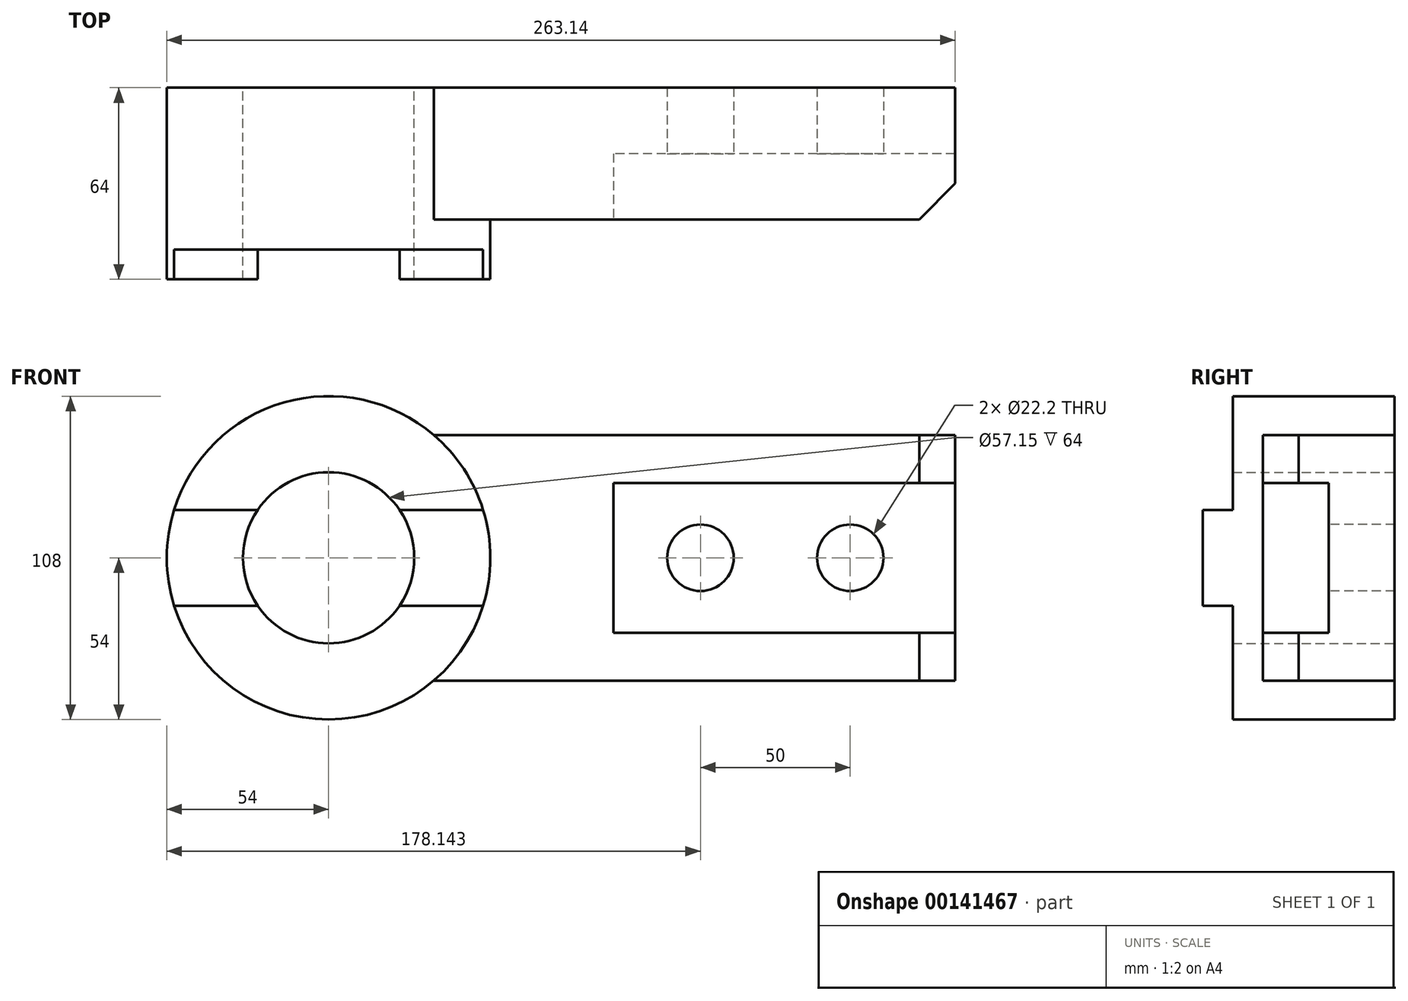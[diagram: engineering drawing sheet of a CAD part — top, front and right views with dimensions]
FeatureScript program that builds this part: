
annotation { "Feature Type Name" : "Feature", "Feature Type Description" : "" }
export const myFeature = defineFeature(function(context is Context, id is Id, definition is map)
    precondition{}
    {
        {
            var Q0;
            Q0=qCreatedBy(makeId("Front.planeOp"),FACE);
            var sketch = newSketch(context, id + "F0", { "sketchPlane" : qUnion([Q0])});
            skCircle(sketch, "E0", {"center": v(0, 0) * mm, "radius": 28.57 * mm});
            skCircle(sketch, "E1", {"center": v(0, 0) * mm, "radius": 54 * mm});
            skLineSegment(sketch, "E2", {"start": v(35.14, 41) * mm, "end": v(209.14, 41) * mm});
            skLineSegment(sketch, "E3", {"start": v(209.14, 41) * mm, "end": v(209.14, -41) * mm});
            skLineSegment(sketch, "E4", {"start": v(209.14, -41) * mm, "end": v(35.14, -41) * mm});
            skSolve(sketch);
        }
        {
            var Q0;
            Q0=makeQuery(id+"F0.imprint","IMPRINT",FACE,{"disambiguationData":[TD([[makeQuery(id+"F0.imprint","IMPRINT",EDGE,{"derivedFrom":sQuery(id+"F0.wireOp",EDGE,"E0")}),-1.0]])]});
            extrude(context, id + "F1", {"entities" : qUnion([Q0]), "depth" : 64 * mm});
        }
        {
            var Q0;
            {var subQ0=sQuery(id+"F0.wireOp",EDGE,"E2");Q0=makeQuery(id+"F0.imprint","IMPRINT",FACE,{"disambiguationData":[TD([[makeQuery(id+"F0.imprint","IMPRINT",EDGE,{"derivedFrom":subQ0}),-1.0]])]});}
            extrude(context, id + "F2", {"entities" : qUnion([Q0]), "operationType" : NewBodyOperationType.ADD, "depth" : 44 * mm});
        }
        {
            var Q0;
            Q0=makeQuery(id+"F2.opExtrude","CAP_FACE",FACE,{"disambiguationData":[OSD([sQuery(id+"F0.wireOp",EDGE,"E1"),sQuery(id+"F0.wireOp",EDGE,"E2"),sQuery(id+"F0.wireOp",EDGE,"E3"),sQuery(id+"F0.wireOp",EDGE,"E4")])],"isStart":false});
            var sketch = newSketch(context, id + "F3", { "sketchPlane" : qUnion([Q0])});
            skLineSegment(sketch, "E5", {"start": v(209.14, -41) * mm, "end": v(209.14, -25) * mm});
            skLineSegment(sketch, "E6", {"start": v(209.14, -25) * mm, "end": v(95.14, -25) * mm});
            skLineSegment(sketch, "E7", {"start": v(95.14, -25) * mm, "end": v(95.14, 25) * mm});
            skLineSegment(sketch, "E8", {"start": v(95.14, 25) * mm, "end": v(209.14, 25) * mm});
            skLineSegment(sketch, "E9", {"start": v(209.14, 25) * mm, "end": v(209.14, 41) * mm});
            skCircle(sketch, "E10", {"center": v(124.14, 0) * mm, "radius": 11.1 * mm});
            skCircle(sketch, "E11", {"center": v(174.14, 0) * mm, "radius": 11.1 * mm});
            skSolve(sketch);
        }
        {
            var Q0;
            Q0=makeQuery(id+"F3.imprint","IMPRINT",FACE,{"disambiguationData":[TD([[makeQuery(id+"F3.imprint","IMPRINT",EDGE,{"derivedFrom":sQuery(id+"F3.wireOp",EDGE,"E11")}),1.0]])]});
            var Q1;
            Q1=makeQuery(id+"F3.imprint","IMPRINT",FACE,{"disambiguationData":[TD([[makeQuery(id+"F3.imprint","IMPRINT",EDGE,{"derivedFrom":sQuery(id+"F3.wireOp",EDGE,"E10")}),1.0]])]});
            extrude(context, id + "F4", {"entities" : qUnion([Q0, Q1]), "operationType" : NewBodyOperationType.REMOVE, "endBound" : BoundingType.THROUGH_ALL, "oppositeDirection" : true, "depth" : 25 * mm});
        }
        {
            var Q0;
            {var subQ1=sQuery(id+"F3.wireOp",EDGE,"E6");Q0=makeQuery(id+"F3.imprint","IMPRINT",FACE,{"disambiguationData":[TD([[makeQuery(id+"F3.imprint","IMPRINT",EDGE,{"derivedFrom":subQ1}),-1.0]])]});}
            extrude(context, id + "F5", {"entities" : qUnion([Q0]), "operationType" : NewBodyOperationType.REMOVE, "oppositeDirection" : true, "depth" : (44 - 22) * mm});
        }
        {
            var Q0;
            Q0=makeQuery(id+"F1.opExtrude","CAP_FACE",FACE,{"disambiguationData":[OSD([sQuery(id+"F0.wireOp",EDGE,"E0"),sQuery(id+"F0.wireOp",EDGE,"E1")])],"isStart":false});
            var sketch = newSketch(context, id + "F6", { "sketchPlane" : qUnion([Q0])});
            skLineSegment(sketch, "E12", {"start": v(-51.58, 16) * mm, "end": v(-23.68, 16) * mm});
            skLineSegment(sketch, "E13.MirrorCS", {"start": v(-51.58, -16) * mm, "end": v(-23.68, -16) * mm});
            skLineSegment(sketch, "E14.MirrorCS", {"start": v(51.58, 16) * mm, "end": v(23.68, 16) * mm});
            skLineSegment(sketch, "E15.MirrorCS", {"start": v(51.58, -16) * mm, "end": v(23.68, -16) * mm});
            skSolve(sketch);
        }
        {
            var Q0;
            {var subQ0=sQuery(id+"F6.wireOp",EDGE,"E12");Q0=makeQuery(id+"F6.imprint","IMPRINT",FACE,{"disambiguationData":[TD([[makeQuery(id+"F6.imprint","IMPRINT",EDGE,{"derivedFrom":subQ0}),1.0]])]});}
            var Q1;
            {var subQ0=sQuery(id+"F6.wireOp",EDGE,"E13.MirrorCS");Q1=makeQuery(id+"F6.imprint","IMPRINT",FACE,{"disambiguationData":[TD([[makeQuery(id+"F6.imprint","IMPRINT",EDGE,{"derivedFrom":subQ0}),-1.0]])]});}
            extrude(context, id + "F7", {"entities" : qUnion([Q0, Q1]), "operationType" : NewBodyOperationType.REMOVE, "oppositeDirection" : true, "depth" : 10 * mm});
        }
        {
            var Q0;
            Q0=makeQuery(id+"F2.opExtrude","SWEPT_FACE",FACE,{"disambiguationData":[OSD([sQuery(id+"F0.wireOp",EDGE,"E2")])]});
            var sketch = newSketch(context, id + "F8", { "sketchPlane" : qUnion([Q0])});
            skLineSegment(sketch, "E16", {"start": v(209.14, -44) * mm, "end": v(197.14, -44) * mm});
            skLineSegment(sketch, "E17", {"start": v(209.14, -44) * mm, "end": v(209.14, -32) * mm});
            skLineSegment(sketch, "E18", {"start": v(209.14, -32) * mm, "end": v(197.14, -44) * mm});
            skSolve(sketch);
        }
        {
            var Q0;
            Q0=makeQuery(id+"F8.imprint","IMPRINT",FACE,{"disambiguationData":[TD([[makeQuery(id+"F8.imprint","IMPRINT",EDGE,{"derivedFrom":sQuery(id+"F8.wireOp",EDGE,"E16")}),1.0]])]});
            extrude(context, id + "F9", {"entities" : qUnion([Q0]), "operationType" : NewBodyOperationType.REMOVE, "endBound" : BoundingType.THROUGH_ALL, "oppositeDirection" : true, "depth" : 25 * mm});
        }
    });
